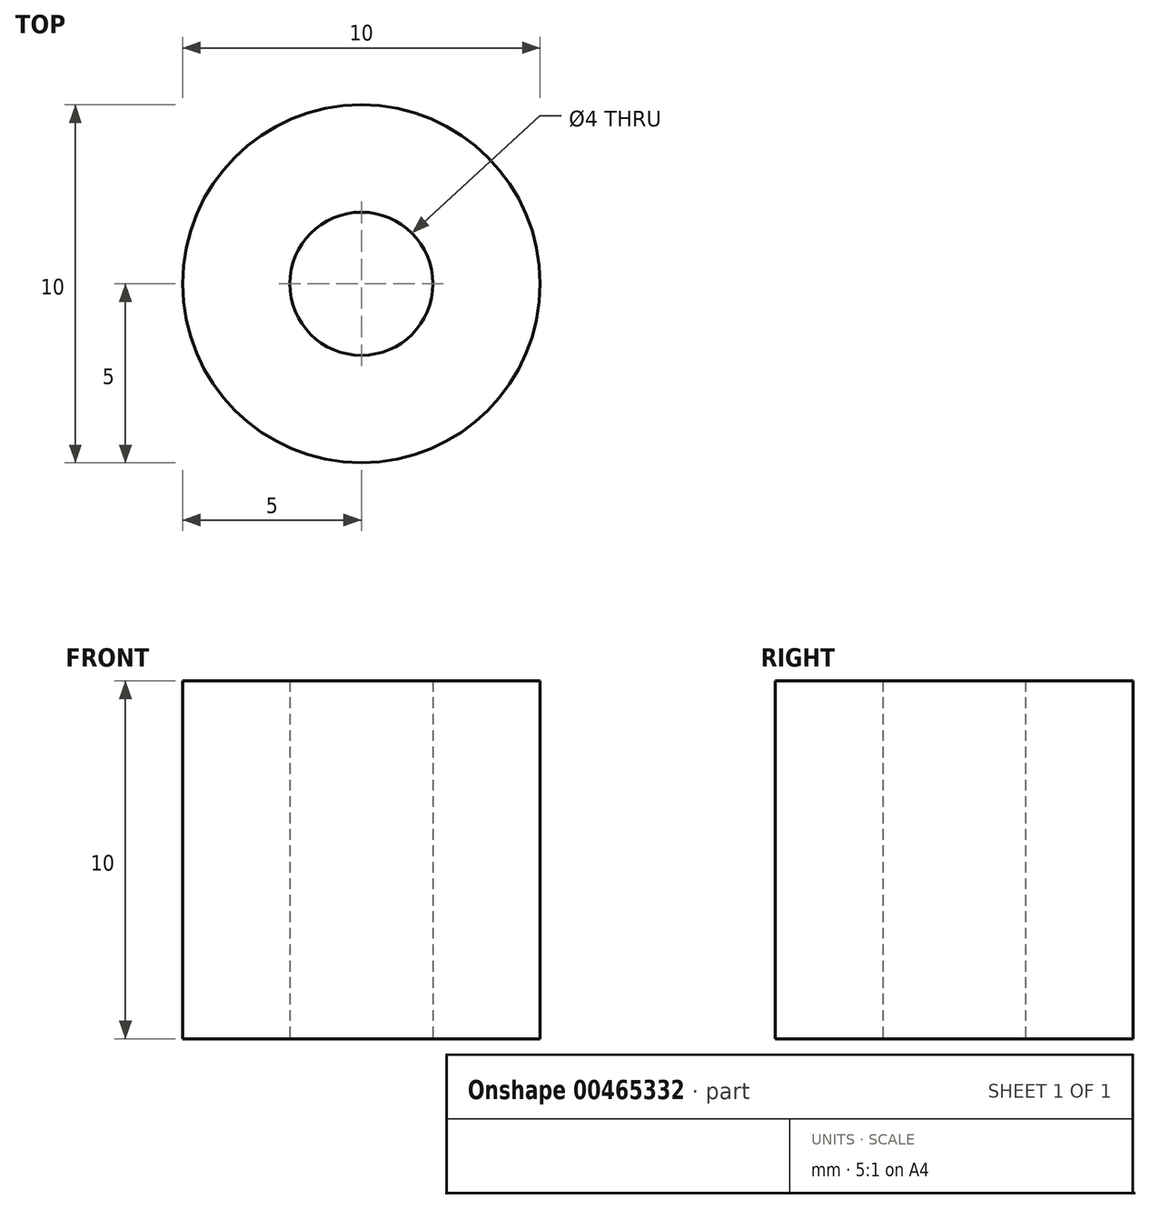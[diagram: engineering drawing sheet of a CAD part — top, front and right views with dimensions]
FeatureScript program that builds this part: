
annotation { "Feature Type Name" : "Feature", "Feature Type Description" : "" }
export const myFeature = defineFeature(function(context is Context, id is Id, definition is map)
    precondition{}
    {
        {
            var Q0;
            Q0=qCreatedBy(makeId("Top.planeOp"),FACE);
            var sketch = newSketch(context, id + "F0", { "sketchPlane" : qUnion([Q0])});
            skCircle(sketch, "E0", {"center": v(0, 0) * mm, "radius": 5 * mm});
            skCircle(sketch, "E1", {"center": v(0, 0) * mm, "radius": 2 * mm});
            skSolve(sketch);
        }
        {
            var Q0;
            Q0 = qSketchRegion(id + "F0", true);
            extrude(context, id + "F1", {"entities" : qUnion([Q0]), "depth" : 10 * mm});
        }
    });
